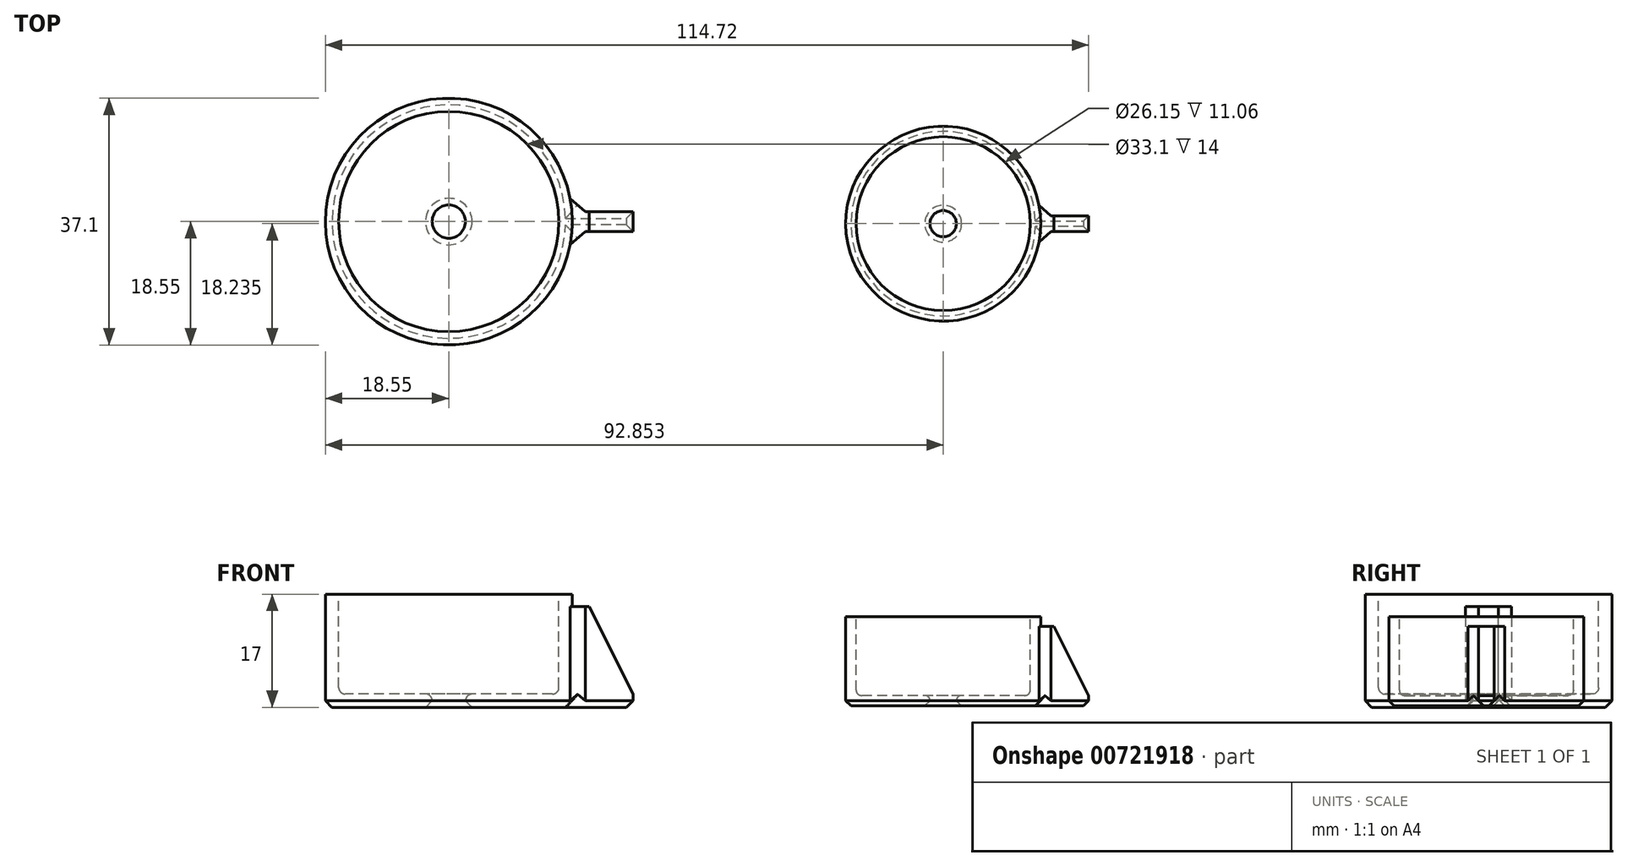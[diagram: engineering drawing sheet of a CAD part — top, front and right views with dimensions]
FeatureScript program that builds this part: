
annotation { "Feature Type Name" : "Feature", "Feature Type Description" : "" }
export const myFeature = defineFeature(function(context is Context, id is Id, definition is map)
    precondition{}
    {
        {
            var Q0;
            Q0=qCreatedBy(makeId("Top.planeOp"),FACE);
            var sketch = newSketch(context, id + "F0", { "sketchPlane" : qUnion([Q0])});
            skCircle(sketch, "E0", {"center": v(0, 0) * mm, "radius": 16.55 * mm, "construction": true});
            skCircle(sketch, "E1", {"center": v(70, 0) * mm, "radius": 13.05 * mm, "construction": true});
            skCircle(sketch, "E2.0", {"center": v(0, 0) * mm, "radius": 18.55 * mm});
            skCircle(sketch, "E3.0", {"center": v(70, 0) * mm, "radius": 15.05 * mm, "construction": true});
            skSolve(sketch);
        }
        {
            var Q0;
            Q0=makeQuery(id+"F0.imprint","IMPRINT",FACE,{"disambiguationData":[TD([[makeQuery(id+"F0.imprint","IMPRINT",EDGE,{"derivedFrom":sQuery(id+"F0.wireOp",EDGE,"E2.0")}),1.0]])]});
            var Q1;
            Q1=makeQuery(id+"F0.imprint","IMPRINT",FACE,{"disambiguationData":[TD([[makeQuery(id+"F0.imprint","IMPRINT",EDGE,{"derivedFrom":sQuery(id+"F0.wireOp",EDGE,"E3.0")}),1.0]])]});
            extrude(context, id + "F1", {"entities" : qUnion([Q0, Q1]), "depth" : 17 * mm, "offsetDistance" : 25 * mm});
        }
        {
            var Q0;
            Q0=sQuery(id+"F0.wireOp",VERTEX,"E2.0.center");
            var Q1;
            Q1=qCreatedBy(makeId("Front.planeOp"),FACE);
            cPlane(context, id + "F2", {"entities" : qUnion([Q0, Q1]), "cplaneType" : CPlaneType.PLANE_POINT, "offset" : 25 * mm, "width" : 150 * mm, "height" : 150 * mm});
        }
        {
            var Q0;
            Q0=qCreatedBy(id+"F2.planeOp",FACE);
            var sketch = newSketch(context, id + "F3", { "sketchPlane" : qUnion([Q0])});
            skLineSegment(sketch, "E4", {"start": v(0, 0) * mm, "end": v(16.55, 0) * mm});
            skLineSegment(sketch, "E5", {"start": v(16.55, 0) * mm, "end": v(27.67, 0) * mm});
            skLineSegment(sketch, "E6", {"start": v(21.1, 15.14) * mm, "end": v(16.73, 15.14) * mm});
            skLineSegment(sketch, "E7", {"start": v(16.73, 15.14) * mm, "end": v(0, 0) * mm});
            skLineSegment(sketch, "E8", {"start": v(27.67, 0) * mm, "end": v(27.67, 2) * mm});
            skLineSegment(sketch, "E9", {"start": v(27.67, 2) * mm, "end": v(21.1, 15.14) * mm});
            skLineSegment(sketch, "E10", {"start": v(0, 0) * mm, "end": v(0, 22.37) * mm});
            skSolve(sketch);
        }
        {
            var Q0;
            Q0=makeQuery(id+"F3.imprint","IMPRINT",FACE,{"disambiguationData":[TD([[makeQuery(id+"F3.imprint","IMPRINT",EDGE,{"derivedFrom":sQuery(id+"F3.wireOp",EDGE,"E4")}),1.0]])]});
            extrude(context, id + "F4", {"entities" : qUnion([Q0]), "operationType" : NewBodyOperationType.ADD, "depth" : 3 * mm, "offsetDistance" : 25 * mm, "symmetric" : true});
        }
        {
            var Q0;
            Q0=makeQuery(id+"F1.opExtrude","CAP_FACE",FACE,{"disambiguationData":[OSD([sQuery(id+"F0.wireOp",EDGE,"E2.0")])],"isStart":false});
            var sketch = newSketch(context, id + "F5", { "sketchPlane" : qUnion([Q0])});
            skCircle(sketch, "E11", {"center": v(0, 0) * mm, "radius": 16.55 * mm});
            skSolve(sketch);
        }
        {
            var Q0;
            Q0=sQuery(id+"F0.wireOp",VERTEX,"E0.center");
            var Q1;
            Q1=makeQuery(id+"F1.opExtrude","SWEPT_BODY",BODY,{"disambiguationData":[OSD([sQuery(id+"F0.wireOp",EDGE,"E2.0")])]});
            hole(context, id + "F6", {"style" : HoleStyle.SIMPLE, "endStyle" : HoleEndStyle.THROUGH, "oppositeDirection" : true, "holeDiameter" : 5 * mm, "majorDiameter" : 5 * mm, "isTappedThrough" : true, "tappedDepth" : 12 * mm, "tapClearance" : 3, "locations" : qUnion([Q0]), "scope" : qUnion([Q1]), "startStyle" : HoleStartStyle.PART});
        }
        {
            var Q0;
            Q0=makeQuery(id+"F5.imprint","IMPRINT",FACE,{"disambiguationData":[TD([[makeQuery(id+"F5.imprint","IMPRINT",EDGE,{"derivedFrom":sQuery(id+"F5.wireOp",EDGE,"E11")}),1.0]])]});
            extrude(context, id + "F7", {"entities" : qUnion([Q0]), "operationType" : NewBodyOperationType.REMOVE, "oppositeDirection" : true, "depth" : 15 * mm, "offsetDistance" : 25 * mm});
        }
        {
            var Q0;
            Q0=makeQuery(id+"F7.boolean.opBoolean","COPY",EDGE,{"derivedFrom":makeQuery(id+"F7.opExtrude","CAP_EDGE",EDGE,{"disambiguationData":[OSD([sQuery(id+"F5.wireOp",EDGE,"E11")])],"isStart":true})});
            var Q1;
            {var subQ0=sQuery(id+"F3.wireOp",EDGE,"E5");var subQ1=sQuery(id+"F3.wireOp",EDGE,"E4");Q1=makeQuery(id+"Fj3pVcfFpI31mhj_1.3.F4.boolean.opBoolean","MERGE",FACE,{"derivedFrom":[makeQuery(id+"Fj3pVcfFpI31mhj_1.2.F4.boolean.opBoolean","MERGE",FACE,{"derivedFrom":[makeQuery(id+"Fj3pVcfFpI31mhj_1.1.F4.boolean.opBoolean","MERGE",FACE,{"derivedFrom":[makeQuery(id+"F4.boolean.opBoolean","MERGE",FACE,{"derivedFrom":[makeQuery(id+"F1.opExtrude","CAP_FACE",FACE,{"disambiguationData":[OSD([sQuery(id+"F0.wireOp",EDGE,"E2.0")])],"isStart":true}),makeQuery(id+"F4.opExtrude","SWEPT_FACE",FACE,{"disambiguationData":[OSD([subQ1,subQ0])]})]}),makeQuery(id+"Fj3pVcfFpI31mhj_1.1.F4.opExtrude","SWEPT_FACE",FACE,{"disambiguationData":[OSD([subQ1,subQ0])]})]}),makeQuery(id+"Fj3pVcfFpI31mhj_1.2.F4.opExtrude","SWEPT_FACE",FACE,{"disambiguationData":[OSD([subQ1,subQ0])]})]}),makeQuery(id+"Fj3pVcfFpI31mhj_1.3.F4.opExtrude","SWEPT_FACE",FACE,{"disambiguationData":[OSD([subQ1,subQ0])]})]});}
            chamfer(context, id + "F8", {"entities" : qUnion([Q0, Q1]), "width" : 1 * mm, "tangentPropagation" : true});
        }
        {
            var Q0;
            Q0=makeQuery(id+"Fj3pVcfFpI31mhj_1.2.F4.boolean.opBoolean","INTERSECT",EDGE,{"derivedFrom":[makeQuery(id+"F1.opExtrude","SWEPT_FACE",FACE,{"disambiguationData":[OSD([sQuery(id+"F0.wireOp",EDGE,"E2.0")])]}),makeQuery(id+"Fj3pVcfFpI31mhj_1.2.F4.opExtrude","CAP_FACE",FACE,{"disambiguationData":[OSD([sQuery(id+"F3.wireOp",EDGE,"E4"),sQuery(id+"F3.wireOp",EDGE,"E5"),sQuery(id+"F3.wireOp",EDGE,"E6"),sQuery(id+"F3.wireOp",EDGE,"E7"),sQuery(id+"F3.wireOp",EDGE,"E8"),sQuery(id+"F3.wireOp",EDGE,"E9")])],"isStart":false})]});
            var Q1;
            Q1=makeQuery(id+"Fj3pVcfFpI31mhj_1.1.F4.boolean.opBoolean","INTERSECT",EDGE,{"derivedFrom":[makeQuery(id+"F1.opExtrude","SWEPT_FACE",FACE,{"disambiguationData":[OSD([sQuery(id+"F0.wireOp",EDGE,"E2.0")])]}),makeQuery(id+"Fj3pVcfFpI31mhj_1.1.F4.opExtrude","CAP_FACE",FACE,{"disambiguationData":[OSD([sQuery(id+"F3.wireOp",EDGE,"E4"),sQuery(id+"F3.wireOp",EDGE,"E5"),sQuery(id+"F3.wireOp",EDGE,"E6"),sQuery(id+"F3.wireOp",EDGE,"E7"),sQuery(id+"F3.wireOp",EDGE,"E8"),sQuery(id+"F3.wireOp",EDGE,"E9")])],"isStart":true})]});
            var Q2;
            Q2=makeQuery(id+"Fj3pVcfFpI31mhj_1.2.F4.boolean.opBoolean","INTERSECT",EDGE,{"derivedFrom":[makeQuery(id+"F1.opExtrude","SWEPT_FACE",FACE,{"disambiguationData":[OSD([sQuery(id+"F0.wireOp",EDGE,"E2.0")])]}),makeQuery(id+"Fj3pVcfFpI31mhj_1.2.F4.opExtrude","CAP_FACE",FACE,{"disambiguationData":[OSD([sQuery(id+"F3.wireOp",EDGE,"E4"),sQuery(id+"F3.wireOp",EDGE,"E5"),sQuery(id+"F3.wireOp",EDGE,"E6"),sQuery(id+"F3.wireOp",EDGE,"E7"),sQuery(id+"F3.wireOp",EDGE,"E8"),sQuery(id+"F3.wireOp",EDGE,"E9")])],"isStart":true})]});
            var Q3;
            Q3=makeQuery(id+"Fj3pVcfFpI31mhj_1.3.F4.boolean.opBoolean","INTERSECT",EDGE,{"derivedFrom":[makeQuery(id+"F1.opExtrude","SWEPT_FACE",FACE,{"disambiguationData":[OSD([sQuery(id+"F0.wireOp",EDGE,"E2.0")])]}),makeQuery(id+"Fj3pVcfFpI31mhj_1.3.F4.opExtrude","CAP_FACE",FACE,{"disambiguationData":[OSD([sQuery(id+"F3.wireOp",EDGE,"E4"),sQuery(id+"F3.wireOp",EDGE,"E5"),sQuery(id+"F3.wireOp",EDGE,"E6"),sQuery(id+"F3.wireOp",EDGE,"E7"),sQuery(id+"F3.wireOp",EDGE,"E8"),sQuery(id+"F3.wireOp",EDGE,"E9")])],"isStart":false})]});
            var Q4;
            Q4=makeQuery(id+"Fj3pVcfFpI31mhj_1.3.F4.boolean.opBoolean","INTERSECT",EDGE,{"derivedFrom":[makeQuery(id+"F1.opExtrude","SWEPT_FACE",FACE,{"disambiguationData":[OSD([sQuery(id+"F0.wireOp",EDGE,"E2.0")])]}),makeQuery(id+"Fj3pVcfFpI31mhj_1.3.F4.opExtrude","CAP_FACE",FACE,{"disambiguationData":[OSD([sQuery(id+"F3.wireOp",EDGE,"E4"),sQuery(id+"F3.wireOp",EDGE,"E5"),sQuery(id+"F3.wireOp",EDGE,"E6"),sQuery(id+"F3.wireOp",EDGE,"E7"),sQuery(id+"F3.wireOp",EDGE,"E8"),sQuery(id+"F3.wireOp",EDGE,"E9")])],"isStart":true})]});
            var Q5;
            Q5=makeQuery(id+"F4.boolean.opBoolean","INTERSECT",EDGE,{"derivedFrom":[makeQuery(id+"F1.opExtrude","SWEPT_FACE",FACE,{"disambiguationData":[OSD([sQuery(id+"F0.wireOp",EDGE,"E2.0")])]}),makeQuery(id+"F4.opExtrude","CAP_FACE",FACE,{"disambiguationData":[OSD([sQuery(id+"F3.wireOp",EDGE,"E4"),sQuery(id+"F3.wireOp",EDGE,"E5"),sQuery(id+"F3.wireOp",EDGE,"E6"),sQuery(id+"F3.wireOp",EDGE,"E7"),sQuery(id+"F3.wireOp",EDGE,"E8"),sQuery(id+"F3.wireOp",EDGE,"E9")])],"isStart":false})]});
            var Q6;
            Q6=makeQuery(id+"F4.boolean.opBoolean","INTERSECT",EDGE,{"derivedFrom":[makeQuery(id+"F1.opExtrude","SWEPT_FACE",FACE,{"disambiguationData":[OSD([sQuery(id+"F0.wireOp",EDGE,"E2.0")])]}),makeQuery(id+"F4.opExtrude","CAP_FACE",FACE,{"disambiguationData":[OSD([sQuery(id+"F3.wireOp",EDGE,"E4"),sQuery(id+"F3.wireOp",EDGE,"E5"),sQuery(id+"F3.wireOp",EDGE,"E6"),sQuery(id+"F3.wireOp",EDGE,"E7"),sQuery(id+"F3.wireOp",EDGE,"E8"),sQuery(id+"F3.wireOp",EDGE,"E9")])],"isStart":true})]});
            var Q7;
            Q7=makeQuery(id+"Fj3pVcfFpI31mhj_1.1.F4.boolean.opBoolean","INTERSECT",EDGE,{"derivedFrom":[makeQuery(id+"F1.opExtrude","SWEPT_FACE",FACE,{"disambiguationData":[OSD([sQuery(id+"F0.wireOp",EDGE,"E2.0")])]}),makeQuery(id+"Fj3pVcfFpI31mhj_1.1.F4.opExtrude","CAP_FACE",FACE,{"disambiguationData":[OSD([sQuery(id+"F3.wireOp",EDGE,"E4"),sQuery(id+"F3.wireOp",EDGE,"E5"),sQuery(id+"F3.wireOp",EDGE,"E6"),sQuery(id+"F3.wireOp",EDGE,"E7"),sQuery(id+"F3.wireOp",EDGE,"E8"),sQuery(id+"F3.wireOp",EDGE,"E9")])],"isStart":false})]});
            chamfer(context, id + "F9", {"entities" : qUnion([Q0, Q1, Q2, Q3, Q4, Q5, Q6, Q7]), "width" : 2 * mm, "tangentPropagation" : true});
        }
        {
            var Q0;
            Q0=makeQuery(id+"F7.boolean.opBoolean","COPY",FACE,{"derivedFrom":makeQuery(id+"F7.opExtrude","CAP_FACE",FACE,{"disambiguationData":[OSD([sQuery(id+"F5.wireOp",EDGE,"E11")])],"isStart":false})});
            fillet(context, id + "F10", {"entities" : qUnion([Q0]), "tangentPropagation" : true, "radius" : 1 * mm, "defaultsChanged" : false, "vertexSettings" : [], "allowEdgeOverflow" : false});
        }
        {
            var Q0;
            Q0=makeQuery(id+"F1.opExtrude","SWEPT_BODY",BODY,{"disambiguationData":[OSD([sQuery(id+"F0.wireOp",EDGE,"E2.0")])]});
            transform(context, id + "F11", {"entities" : qUnion([Q0]), "transformType" : TransformType.TRANSLATION_3D, "dx" : 70 * mm, "dy" : 0 * mm, "dz" : 0 * mm, "makeCopy" : true});
        }
        {
            var Q0;
            Q0=makeQuery(id+"F11.opPattern","COPY",BODY,{"derivedFrom":makeQuery(id+"F1.opExtrude","SWEPT_BODY",BODY,{"disambiguationData":[OSD([sQuery(id+"F0.wireOp",EDGE,"E2.0")])]}),"instanceName":"1"});
            var Q1;
            {var subQ0=sQuery(id+"F3.wireOp",EDGE,"E5");var subQ1=sQuery(id+"F3.wireOp",EDGE,"E4");var subQ2=makeQuery(id+"F4.opExtrude","CAP_FACE",FACE,{"disambiguationData":[OSD([subQ1,subQ0,sQuery(id+"F3.wireOp",EDGE,"E6"),sQuery(id+"F3.wireOp",EDGE,"E7"),sQuery(id+"F3.wireOp",EDGE,"E8"),sQuery(id+"F3.wireOp",EDGE,"E9")])],"isStart":false});Q1=makeQuery(id+"F11.opPattern","COPY",VERTEX,{"derivedFrom":makeQuery(id+"F9.opChamfer","BLEND_VERTEX",VERTEX,{"blendedFrom":[makeQuery(id+"F4.boolean.opBoolean","INTERSECT",EDGE,{"derivedFrom":[makeQuery(id+"F1.opExtrude","SWEPT_FACE",FACE,{"disambiguationData":[OSD([sQuery(id+"F0.wireOp",EDGE,"E2.0")])]}),subQ2]}),makeQuery(id+"F8.opChamfer","BLEND_FACE",FACE,{"disambiguationData":[OSD([subQ1,subQ0]),TDD([makeQuery(id+"F4.opExtrude","CAP_EDGE",EDGE,{"disambiguationData":[OSD([subQ1,subQ0])],"isStart":false})])]}),subQ2],"blendedInto":[makeQuery(id+"F8.opChamfer","BLEND_FACE",FACE,{"disambiguationData":[OSD([subQ1,subQ0]),TDD([makeQuery(id+"F4.opExtrude","CAP_EDGE",EDGE,{"disambiguationData":[OSD([subQ1,subQ0])],"isStart":false})])]}),subQ2]}),"instanceName":"1"});}
            transform(context, id + "F12", {"entities" : qUnion([Q0]), "transformType" : TransformType.SCALE_UNIFORMLY, "scale" : 0.79, "scalePoint" : qUnion([Q1]), "makeCopy" : false});
        }
    });
